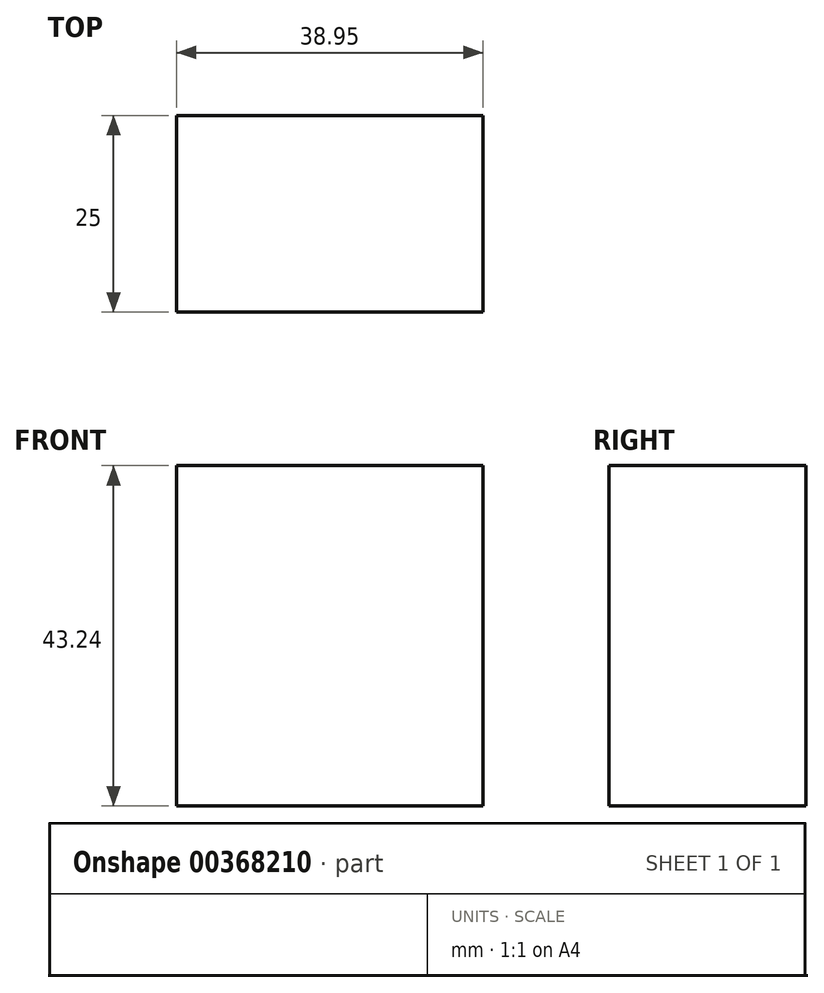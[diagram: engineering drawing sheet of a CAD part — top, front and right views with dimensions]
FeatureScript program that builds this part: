
annotation { "Feature Type Name" : "Feature", "Feature Type Description" : "" }
export const myFeature = defineFeature(function(context is Context, id is Id, definition is map)
    precondition{}
    {
        {
            var Q0;
            Q0=qCreatedBy(makeId("Front.planeOp"),FACE);
            var sketch = newSketch(context, id + "F0", { "sketchPlane" : qUnion([Q0])});
            skLineSegment(sketch, "E0.bottom", {"start": v(-26.11, 51.73) * mm, "end": v(12.84, 51.73) * mm});
            skLineSegment(sketch, "E0.top", {"start": v(-26.11, 8.5) * mm, "end": v(12.84, 8.5) * mm});
            skLineSegment(sketch, "E0.left", {"start": v(-26.11, 51.73) * mm, "end": v(-26.11, 8.5) * mm});
            skLineSegment(sketch, "E0.right", {"start": v(12.84, 51.73) * mm, "end": v(12.84, 8.5) * mm});
            skSolve(sketch);
        }
        {
            var Q0;
            Q0=makeQuery(id+"F0.imprint","IMPRINT",FACE,{"disambiguationData":[TD([[makeQuery(id+"F0.imprint","IMPRINT",EDGE,{"derivedFrom":sQuery(id+"F0.wireOp",EDGE,"E0.bottom")}),-1.0]])]});
            extrude(context, id + "F1", {"entities" : qUnion([Q0]), "depth" : 25 * mm});
        }
    });
